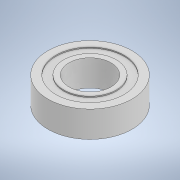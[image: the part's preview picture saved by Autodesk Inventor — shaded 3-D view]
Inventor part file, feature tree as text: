
AUTODESK INVENTOR PART (.ipt)
format: ipt  version: 2020 (Build 240168000, 168)  size: 132,608 bytes
history: native  units: mm
features: extrude x3, sketch x3, projected_geometry x1
ambient origin geometry x8: Origin, YZ Plane, XZ Plane, XY Plane, X Axis, Y Axis, Z Axis, Center Point
bodies: Solid1 (feature_tree)
feature tree (7):
  extrude  "Extrusion1"  Depth=8.0mm
  extrude  "Extrusion2"  Depth=10.0mm
  extrude  "Extrusion3"  Depth=0.2mm TaperAngle=0.0deg
  sketch  "Sketch1"  dims[d0=8.0mm d1=16.0mm]
  sketch  "Sketch2"  dims[d2=5.0mm d3=0.0mm d4=10.0mm]
  projected_geometry  "Projected Loop1"
  sketch  "Sketch3"  dims[d5=13.0mm d6=0.2mm d7=0.0mm d8=0.2mm d9=0.0mm]
